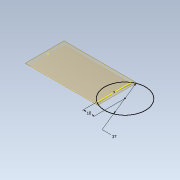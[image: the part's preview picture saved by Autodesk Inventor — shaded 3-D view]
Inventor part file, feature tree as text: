
AUTODESK INVENTOR PART (.ipt)
format: ipt  version: 2021 (Build 250183000, 183)  size: 116,224 bytes
history: native  units: mm
features: other x4, sketch x4, plane x1, extrude x1, hole x1, projected_geometry x1
ambient origin geometry x8: Origin, YZ Plane, XZ Plane, XY Plane, X Axis, Y Axis, Z Axis, Center Point
bodies: Body1 (feature_tree), Body2 (feature_tree)
feature tree (12):
  other  "Sólido1"
  other  "Superficie reglada1"
  other  "Engrosado1"
  plane  "Plano de trabajo1"
  sketch  "Boceto2"  dims[d2=60.0mm d3=0.0mm d4=1.0mm]
  extrude  "Extrusión1"  TaperAngle=15.0deg  [1 undecoded]
  hole  "Agujero1"  [1 undecoded]
  sketch  "Boceto1"  dims[d0=122.0mm d1=15.0deg]
  other  "Sup1"
  sketch  "Boceto3"  dims[d5=1.0mm]
  sketch  "Boceto4"  dims[d8=37.0mm d9=10.0mm d10=0.0mm d11=0.0mm d12=20.0mm d13=3.4mm d14=72.0mm d15=6.3mm d16=2.0mm d17=90.0deg d18=8.0mm d19=20.594885mm]
  projected_geometry  "Contorno proyectado1"
note: 2 required parameter values undecoded (feature->parameter linkage not recoverable at this tier; creation-order binding heuristic only, values carry confidence <= 0.55)
